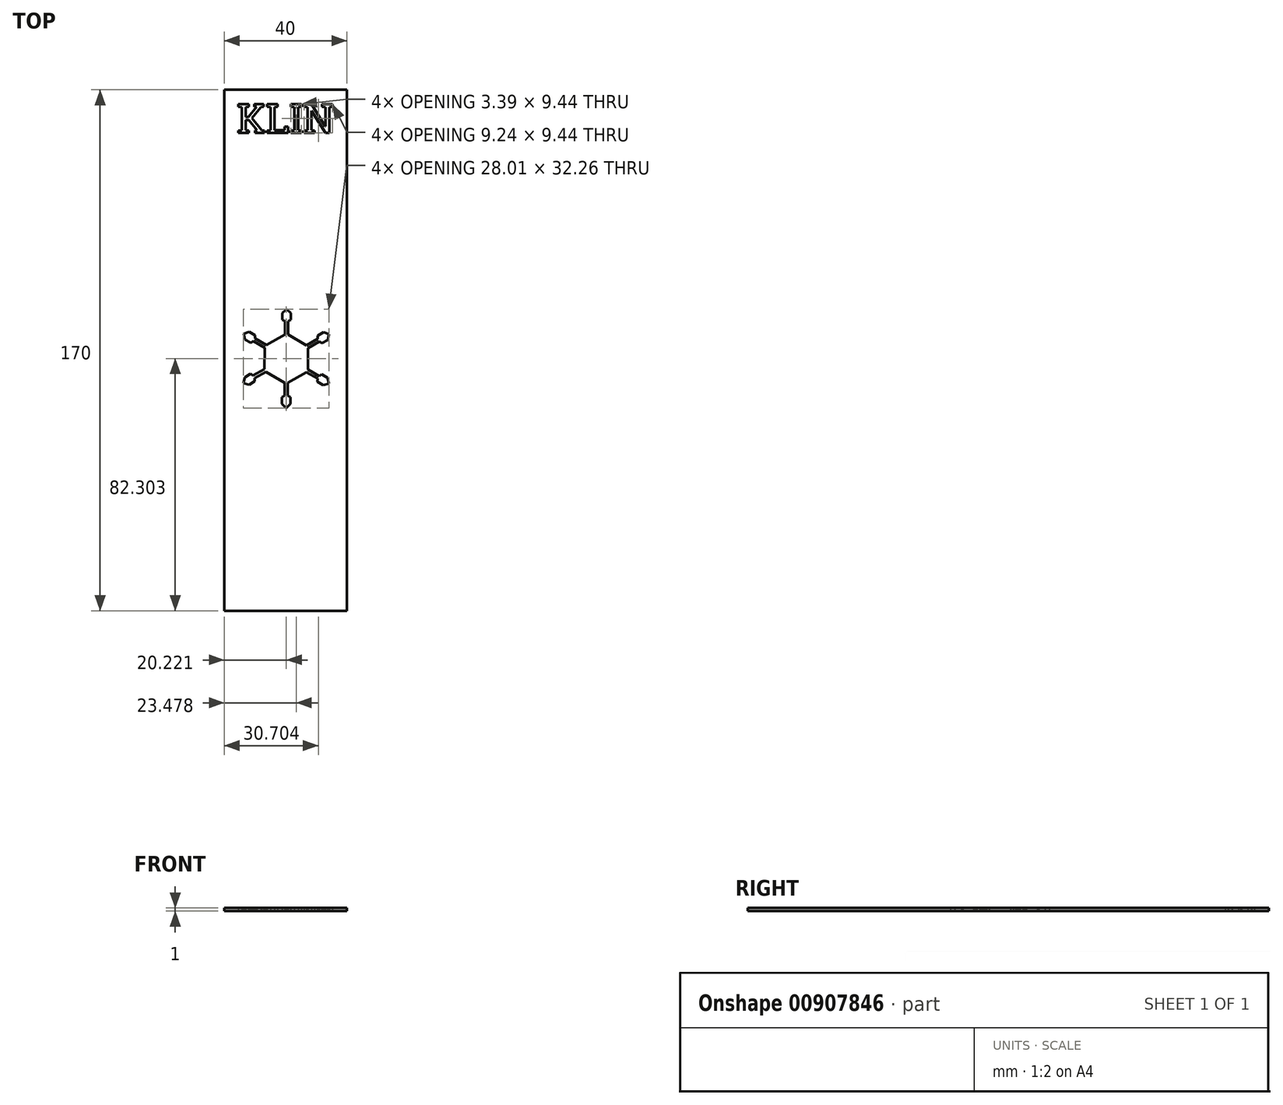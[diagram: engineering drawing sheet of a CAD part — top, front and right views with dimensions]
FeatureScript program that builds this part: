
annotation { "Feature Type Name" : "Feature", "Feature Type Description" : "" }
export const myFeature = defineFeature(function(context is Context, id is Id, definition is map)
    precondition{}
    {
        {
            var Q0;
            Q0=qCreatedBy(makeId("Top.planeOp"),FACE);
            var sketch = newSketch(context, id + "F0", { "sketchPlane" : qUnion([Q0])});
            skLineSegment(sketch, "E0.bottom", {"start": v(-24.74, 110.56) * mm, "end": v(15.26, 110.56) * mm});
            skLineSegment(sketch, "E0.top", {"start": v(-24.74, -59.44) * mm, "end": v(15.26, -59.44) * mm});
            skLineSegment(sketch, "E0.left", {"start": v(-24.74, 110.56) * mm, "end": v(-24.74, -59.44) * mm});
            skLineSegment(sketch, "E0.right", {"start": v(15.26, 110.56) * mm, "end": v(15.26, -59.44) * mm});
            skText(sketch, "E1", { "text": "KLIN\n", "fontName": "RobotoSlab-Regular.ttf"});
            skCircle(sketch, "E2.cCircle", {"center": v(-4.52, 22.86) * mm, "radius": 7.08 * mm, "construction": true});
            skLineSegment(sketch, "E2.0", {"start": v(-11.05, 27.3) * mm, "end": v(-4.95, 30.75) * mm});
            skLineSegment(sketch, "E2.1", {"start": v(-3.93, 30.74) * mm, "end": v(2.1, 27.19) * mm});
            skLineSegment(sketch, "E2.2", {"start": v(2.6, 26.3) * mm, "end": v(2.53, 19.3) * mm});
            skLineSegment(sketch, "E2.3", {"start": v(2.01, 18.42) * mm, "end": v(-4.08, 14.97) * mm});
            skLineSegment(sketch, "E2.4", {"start": v(-5.1, 14.98) * mm, "end": v(-11.14, 18.54) * mm});
            skLineSegment(sketch, "E2.5", {"start": v(-11.63, 19.43) * mm, "end": v(-11.57, 26.43) * mm});
            skPoint(sketch, "E2.0.midPoint", {"position": v(-8, 29.03) * mm});
            skLineSegment(sketch, "E3", {"start": v(-4.95, 30.75) * mm, "end": v(-4.95, 35) * mm});
            skLineSegment(sketch, "E4", {"start": v(-4.95, 35) * mm, "end": v(-5.84, 35.48) * mm});
            skLineSegment(sketch, "E5", {"start": v(-5.84, 35.48) * mm, "end": v(-5.84, 37.64) * mm});
            skLineSegment(sketch, "E6", {"start": v(-5.84, 37.64) * mm, "end": v(-4.44, 39) * mm});
            skLineSegment(sketch, "E7", {"start": v(-4.44, 31.04) * mm, "end": v(-4.44, 39) * mm, "construction": true});
            skLineSegment(sketch, "E8.MirrorCS", {"start": v(-3.05, 35.48) * mm, "end": v(-3.05, 37.64) * mm});
            skLineSegment(sketch, "E9.MirrorCS", {"start": v(-3.05, 37.64) * mm, "end": v(-4.44, 39) * mm});
            skLineSegment(sketch, "E10.MirrorCS", {"start": v(-3.93, 35) * mm, "end": v(-3.05, 35.48) * mm});
            skLineSegment(sketch, "E11.1.0", {"start": v(-11.57, 26.43) * mm, "end": v(-15.25, 28.56) * mm});
            skLineSegment(sketch, "E11.1.1", {"start": v(-15.25, 28.56) * mm, "end": v(-16.1, 28.03) * mm});
            skLineSegment(sketch, "E11.1.2", {"start": v(-16.1, 28.03) * mm, "end": v(-17.97, 29.1) * mm});
            skLineSegment(sketch, "E11.1.3", {"start": v(-17.97, 29.1) * mm, "end": v(-18.45, 31) * mm});
            skLineSegment(sketch, "E11.1.4", {"start": v(-16.58, 31.52) * mm, "end": v(-18.45, 31) * mm});
            skLineSegment(sketch, "E11.1.5", {"start": v(-14.71, 30.45) * mm, "end": v(-16.58, 31.52) * mm});
            skLineSegment(sketch, "E11.1.6", {"start": v(-14.74, 29.44) * mm, "end": v(-14.71, 30.45) * mm});
            skLineSegment(sketch, "E11.2.0", {"start": v(-11.14, 18.54) * mm, "end": v(-14.82, 16.42) * mm});
            skLineSegment(sketch, "E11.2.1", {"start": v(-14.82, 16.42) * mm, "end": v(-14.79, 15.4) * mm});
            skLineSegment(sketch, "E11.2.2", {"start": v(-14.79, 15.4) * mm, "end": v(-16.65, 14.33) * mm});
            skLineSegment(sketch, "E11.2.3", {"start": v(-16.65, 14.33) * mm, "end": v(-18.52, 14.86) * mm});
            skLineSegment(sketch, "E11.2.4", {"start": v(-18.05, 16.75) * mm, "end": v(-18.52, 14.86) * mm});
            skLineSegment(sketch, "E11.2.5", {"start": v(-16.18, 17.83) * mm, "end": v(-18.05, 16.75) * mm});
            skLineSegment(sketch, "E11.2.6", {"start": v(-15.33, 17.3) * mm, "end": v(-16.18, 17.83) * mm});
            skLineSegment(sketch, "E11.3.0", {"start": v(-4.08, 14.97) * mm, "end": v(-4.08, 10.72) * mm});
            skLineSegment(sketch, "E11.3.1", {"start": v(-4.08, 10.72) * mm, "end": v(-3.2, 10.24) * mm});
            skLineSegment(sketch, "E11.3.2", {"start": v(-3.2, 10.24) * mm, "end": v(-3.2, 8.09) * mm});
            skLineSegment(sketch, "E11.3.3", {"start": v(-3.2, 8.09) * mm, "end": v(-4.6, 6.73) * mm});
            skLineSegment(sketch, "E11.3.4", {"start": v(-5.99, 8.09) * mm, "end": v(-4.6, 6.73) * mm});
            skLineSegment(sketch, "E11.3.5", {"start": v(-5.99, 10.24) * mm, "end": v(-5.99, 8.09) * mm});
            skLineSegment(sketch, "E11.3.6", {"start": v(-5.1, 10.72) * mm, "end": v(-5.99, 10.24) * mm});
            skLineSegment(sketch, "E11.4.0", {"start": v(2.53, 19.3) * mm, "end": v(6.21, 17.17) * mm});
            skLineSegment(sketch, "E11.4.1", {"start": v(6.21, 17.17) * mm, "end": v(7.07, 17.7) * mm});
            skLineSegment(sketch, "E11.4.2", {"start": v(7.07, 17.7) * mm, "end": v(8.94, 16.62) * mm});
            skLineSegment(sketch, "E11.4.3", {"start": v(8.94, 16.62) * mm, "end": v(9.41, 14.73) * mm});
            skLineSegment(sketch, "E11.4.4", {"start": v(7.54, 14.2) * mm, "end": v(9.41, 14.73) * mm});
            skLineSegment(sketch, "E11.4.5", {"start": v(5.68, 15.28) * mm, "end": v(7.54, 14.2) * mm});
            skLineSegment(sketch, "E11.4.6", {"start": v(5.7, 16.29) * mm, "end": v(5.68, 15.28) * mm});
            skLineSegment(sketch, "E11.5.0", {"start": v(2.1, 27.19) * mm, "end": v(5.78, 29.31) * mm});
            skLineSegment(sketch, "E11.5.1", {"start": v(5.78, 29.31) * mm, "end": v(5.75, 30.32) * mm});
            skLineSegment(sketch, "E11.5.2", {"start": v(5.75, 30.32) * mm, "end": v(7.61, 31.4) * mm});
            skLineSegment(sketch, "E11.5.3", {"start": v(7.61, 31.4) * mm, "end": v(9.49, 30.86) * mm});
            skLineSegment(sketch, "E11.5.4", {"start": v(9.01, 28.98) * mm, "end": v(9.49, 30.86) * mm});
            skLineSegment(sketch, "E11.5.5", {"start": v(7.15, 27.9) * mm, "end": v(9.01, 28.98) * mm});
            skLineSegment(sketch, "E11.5.6", {"start": v(6.29, 28.43) * mm, "end": v(7.15, 27.9) * mm});
            skLineSegment(sketch, "E12", {"start": v(-15.33, 17.3) * mm, "end": v(-11.63, 19.43) * mm});
            skLineSegment(sketch, "E13", {"start": v(-5.1, 10.72) * mm, "end": v(-5.1, 14.98) * mm});
            skLineSegment(sketch, "E14", {"start": v(5.7, 16.29) * mm, "end": v(2.01, 18.42) * mm});
            skLineSegment(sketch, "E15", {"start": v(6.29, 28.43) * mm, "end": v(2.6, 26.3) * mm});
            skLineSegment(sketch, "E16", {"start": v(-14.74, 29.44) * mm, "end": v(-11.05, 27.3) * mm});
            skPoint(sketch, "E17.orphan", {"position": v(-11.56, 27.02) * mm});
            skPoint(sketch, "E18.MirrorCS.end.orphan", {"position": v(-3.93, 35) * mm});
            skLineSegment(sketch, "E19", {"start": v(-3.93, 35) * mm, "end": v(-3.93, 30.74) * mm});
            const initialGuessF0  = {"E1": [-0.0206, 0.09643, 1, 0, 0.00956]};
            skSetInitialGuess(sketch, initialGuessF0);
            skSolve(sketch);
        }
        {
            var Q0;
            Q0 = qSketchRegion(id + "F0", true);
            extrude(context, id + "F1", {"entities" : qUnion([Q0]), "depth" : 1 * mm, "offsetDistance" : 25 * mm});
        }
    });
